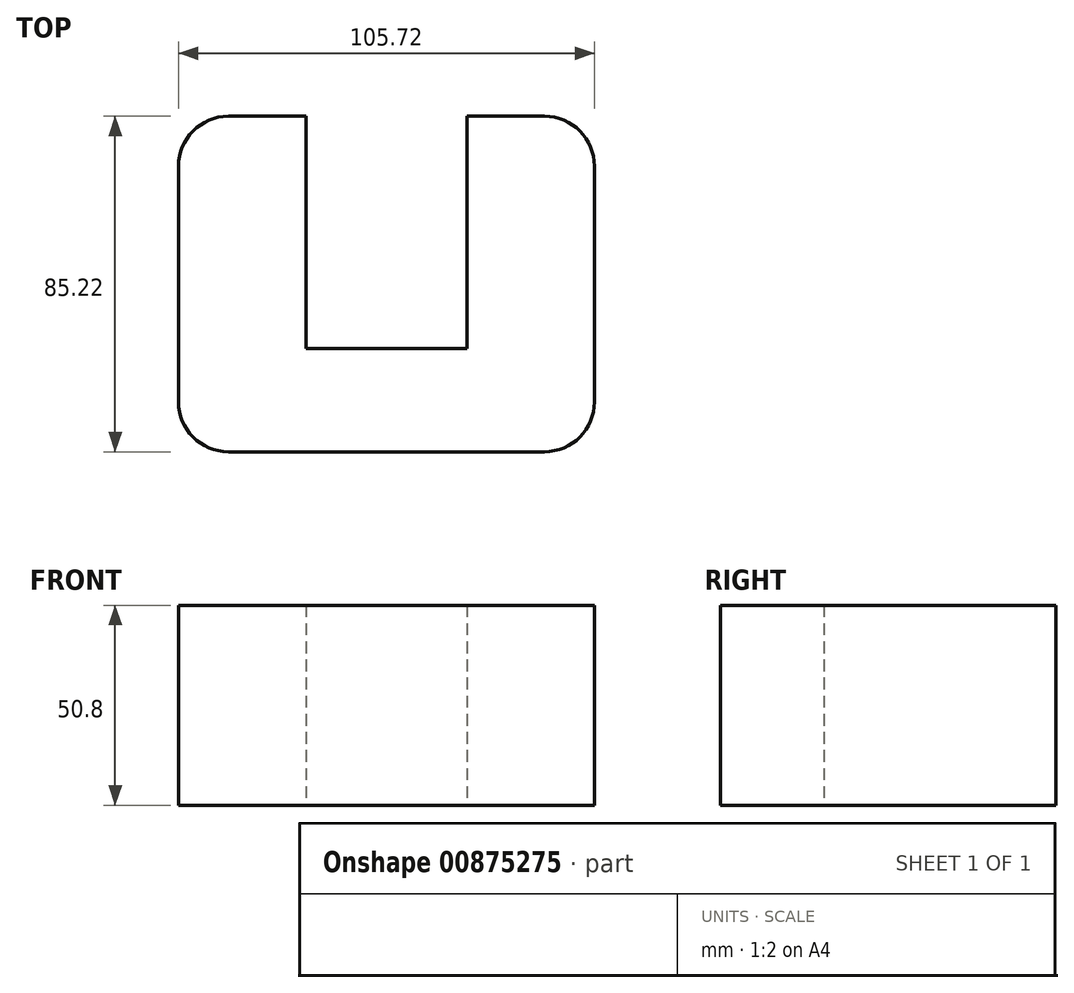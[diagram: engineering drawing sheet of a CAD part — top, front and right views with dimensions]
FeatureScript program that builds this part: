
annotation { "Feature Type Name" : "Feature", "Feature Type Description" : "" }
export const myFeature = defineFeature(function(context is Context, id is Id, definition is map)
    precondition{}
    {
        {
            var Q0;
            Q0=qCreatedBy(makeId("Top.planeOp"),FACE);
            var sketch = newSketch(context, id + "F0", { "sketchPlane" : qUnion([Q0])});
            skLineSegment(sketch, "E0.bottom", {"start": v(-40.16, 42.61) * mm, "end": v(-20.42, 42.61) * mm});
            skLineSegment(sketch, "E0.top", {"start": v(-40.16, -42.61) * mm, "end": v(40.16, -42.61) * mm});
            skLineSegment(sketch, "E0.left", {"start": v(-52.86, 29.91) * mm, "end": v(-52.86, -29.91) * mm});
            skLineSegment(sketch, "E0.right", {"start": v(52.86, 29.91) * mm, "end": v(52.86, -29.91) * mm});
            skPoint(sketch, "E0.middle", {"position": v(0, 0) * mm});
            skPoint(sketch, "E1.visualSharp", {"position": v(-52.86, 42.61) * mm});
            skArc(sketch, "E1.filletArc", {"start": v(-40.16, 42.61) * mm, "mid": v(-49.14, 38.9) * mm, "end": v(-52.86, 29.91) * mm});
            skPoint(sketch, "E2.visualSharp", {"position": v(52.86, 42.61) * mm});
            skArc(sketch, "E2.filletArc", {"start": v(52.86, 29.91) * mm, "mid": v(49.14, 38.9) * mm, "end": v(40.16, 42.61) * mm});
            skPoint(sketch, "E3.visualSharp", {"position": v(-52.86, -42.61) * mm});
            skArc(sketch, "E3.filletArc", {"start": v(-52.86, -29.91) * mm, "mid": v(-49.14, -38.9) * mm, "end": v(-40.16, -42.61) * mm});
            skPoint(sketch, "E4.visualSharp", {"position": v(52.86, -42.61) * mm});
            skArc(sketch, "E4.filletArc", {"start": v(40.16, -42.61) * mm, "mid": v(49.14, -38.9) * mm, "end": v(52.86, -29.91) * mm});
            skLineSegment(sketch, "E5.bottom", {"start": v(-20.42, -16.34) * mm, "end": v(20.42, -16.34) * mm});
            skLineSegment(sketch, "E5.left", {"start": v(-20.42, -16.34) * mm, "end": v(-20.42, 42.61) * mm});
            skLineSegment(sketch, "E5.right", {"start": v(20.42, -16.34) * mm, "end": v(20.42, 42.61) * mm});
            skPoint(sketch, "E5.middle", {"position": v(0, 42.61) * mm});
            skPoint(sketch, "E5.top.end.orphan", {"position": v(20.42, 101.57) * mm});
            skPoint(sketch, "E5.top.start.orphan", {"position": v(-20.42, 101.57) * mm});
            skLineSegment(sketch, "E6.trimOffspring", {"start": v(20.42, 42.61) * mm, "end": v(40.16, 42.61) * mm});
            skSolve(sketch);
        }
        {
            var Q0;
            Q0=makeQuery(id+"F0.imprint","IMPRINT",FACE,{"disambiguationData":[TD([[makeQuery(id+"F0.imprint","IMPRINT",EDGE,{"derivedFrom":sQuery(id+"F0.wireOp",EDGE,"E0.bottom")}),-1.0]])]});
            extrude(context, id + "F1", {"entities" : qUnion([Q0]), "depth" : 50.8 * mm, "offsetDistance" : 25.4 * mm});
        }
    });
